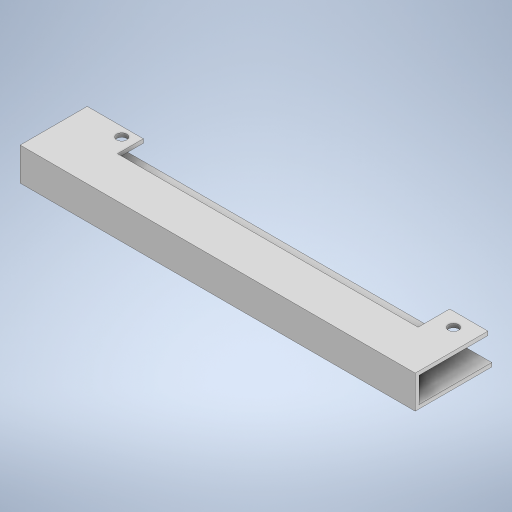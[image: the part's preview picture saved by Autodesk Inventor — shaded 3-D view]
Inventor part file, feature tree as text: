
AUTODESK INVENTOR PART (.ipt)
format: ipt  version: 2023 (Build 270158000, 158)  size: 279,552 bytes
history: native  units: in
note: dims shown in document units (in); Inventor stores cm internally (conversion verified against a paired STEP export)
features: extrude x3, sketch x2
ambient origin geometry x8: Origin, YZ Plane, XZ Plane, XY Plane, X Axis, Y Axis, Z Axis, Center Point
bodies: Solid1 (feature_tree)
feature tree (5):
  sketch  "Sketch1"  dims[d0=0.1043in d1=0.1043in]
  extrude  "Extrusion1"  Depth=0.1043in
  extrude  "Extrusion2"  Depth=0.5768in
  extrude  "Extrusion3"  Depth=0.3937in
  sketch  "Sketch3"  dims[d2=4.0591in d3=0.5768in d4=0.3937in d5=0.7087in d6=0.6496in d7=0.5541in d8=0.4498in d9=0.3839in d10=0.564in d11=0.2096in d12=0.0394in d13=0.0in d14=0.0394in d15=0.2992in d16=0.0in d17=0.0394in d18=0.748in d19=0.0in]
